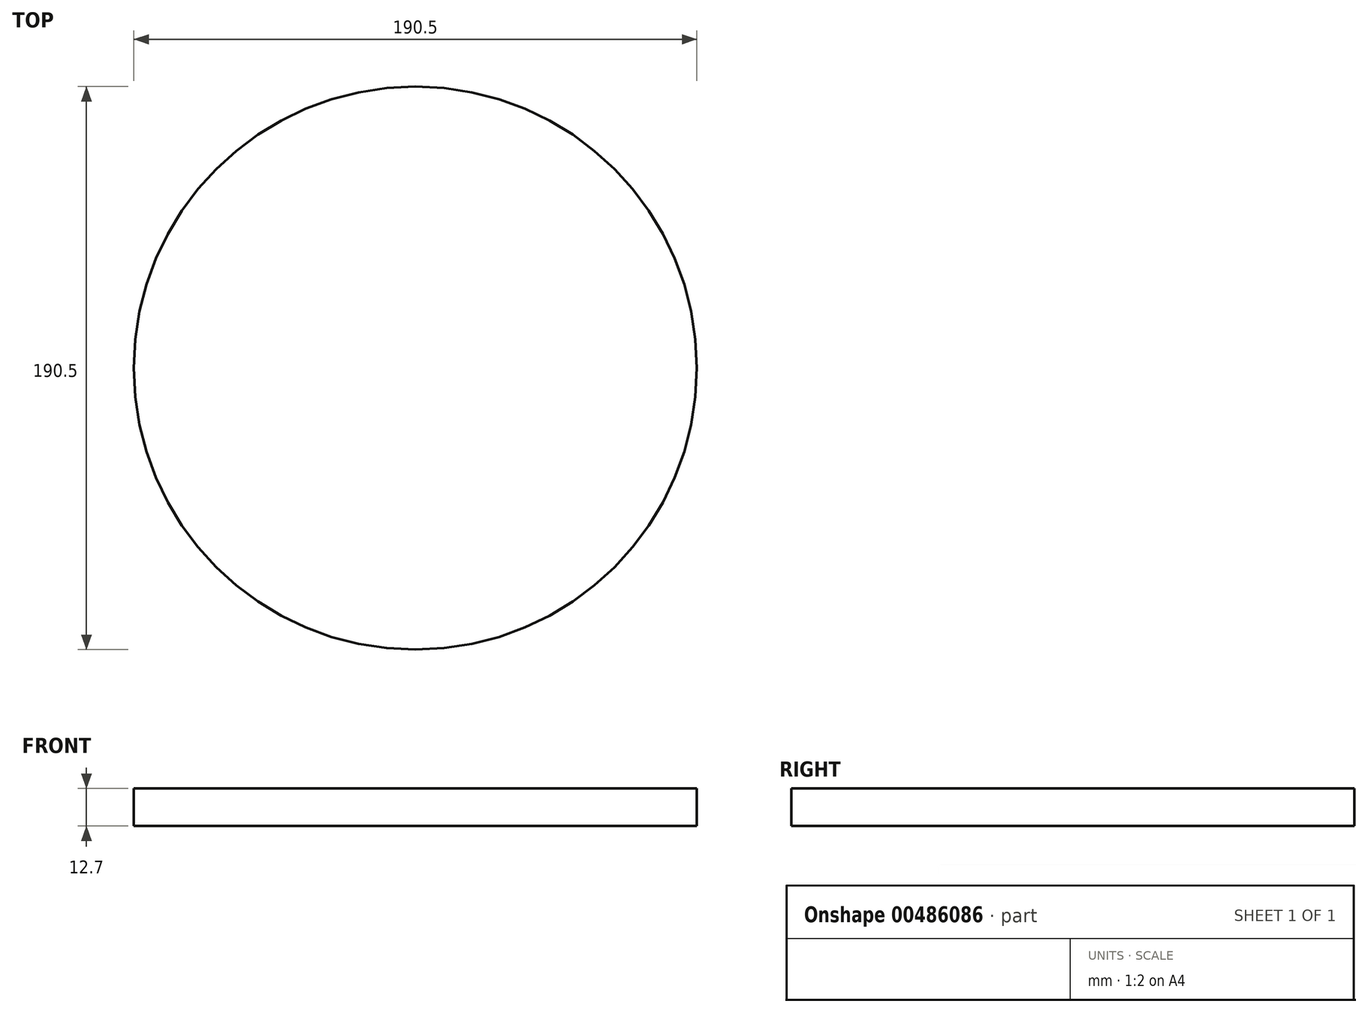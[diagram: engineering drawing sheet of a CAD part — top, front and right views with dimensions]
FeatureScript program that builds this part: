
annotation { "Feature Type Name" : "Feature", "Feature Type Description" : "" }
export const myFeature = defineFeature(function(context is Context, id is Id, definition is map)
    precondition{}
    {
        {
            var Q0;
            Q0=qCreatedBy(makeId("Top.planeOp"),FACE);
            var sketch = newSketch(context, id + "F0", { "sketchPlane" : qUnion([Q0])});
            skCircle(sketch, "E0", {"center": v(0, 0) * mm, "radius": 95.25 * mm});
            skSolve(sketch);
        }
        {
            var Q0;
            Q0 = qSketchRegion(id + "F0", true);
            extrude(context, id + "F1", {"entities" : qUnion([Q0]), "depth" : 12.7 * mm});
        }
    });
